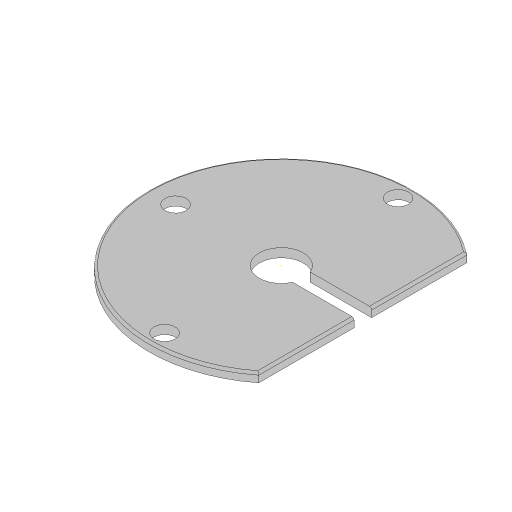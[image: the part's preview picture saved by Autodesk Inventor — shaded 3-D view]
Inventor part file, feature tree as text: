
AUTODESK INVENTOR PART (.ipt)
format: ipt  version: 2023 (Build 270158000, 158)  size: 126,976 bytes
history: native  units: mm
features: sketch x4, extrude x2, fillet x1
ambient origin geometry x8: Origin, YZ Plane, XZ Plane, XY Plane, X Axis, Y Axis, Z Axis, Center Point
bodies: Solid1 (feature_tree)
feature tree (7):
  extrude  "Extrusion1"  Depth=6.0mm
  sketch  "Sketch2"  dims[d2=4.8mm d3=3.5mm d4=3.5mm]
  sketch  "Sketch3"  dims[d5=4.8mm]
  extrude  "Extrusion2"  Depth=3.5mm
  fillet  "Fillet1"  Radius=3.5mm
  sketch  "Sketch1"  dims[d0=60.0mm d1=6.0mm]
  sketch  "Sketch4"  dims[d6=4.8mm d7=10.0mm d8=11.5mm d9=2.0mm d10=0.0mm d17=4.0mm d18=3.0mm d19=0.0mm d20=0.5mm]
